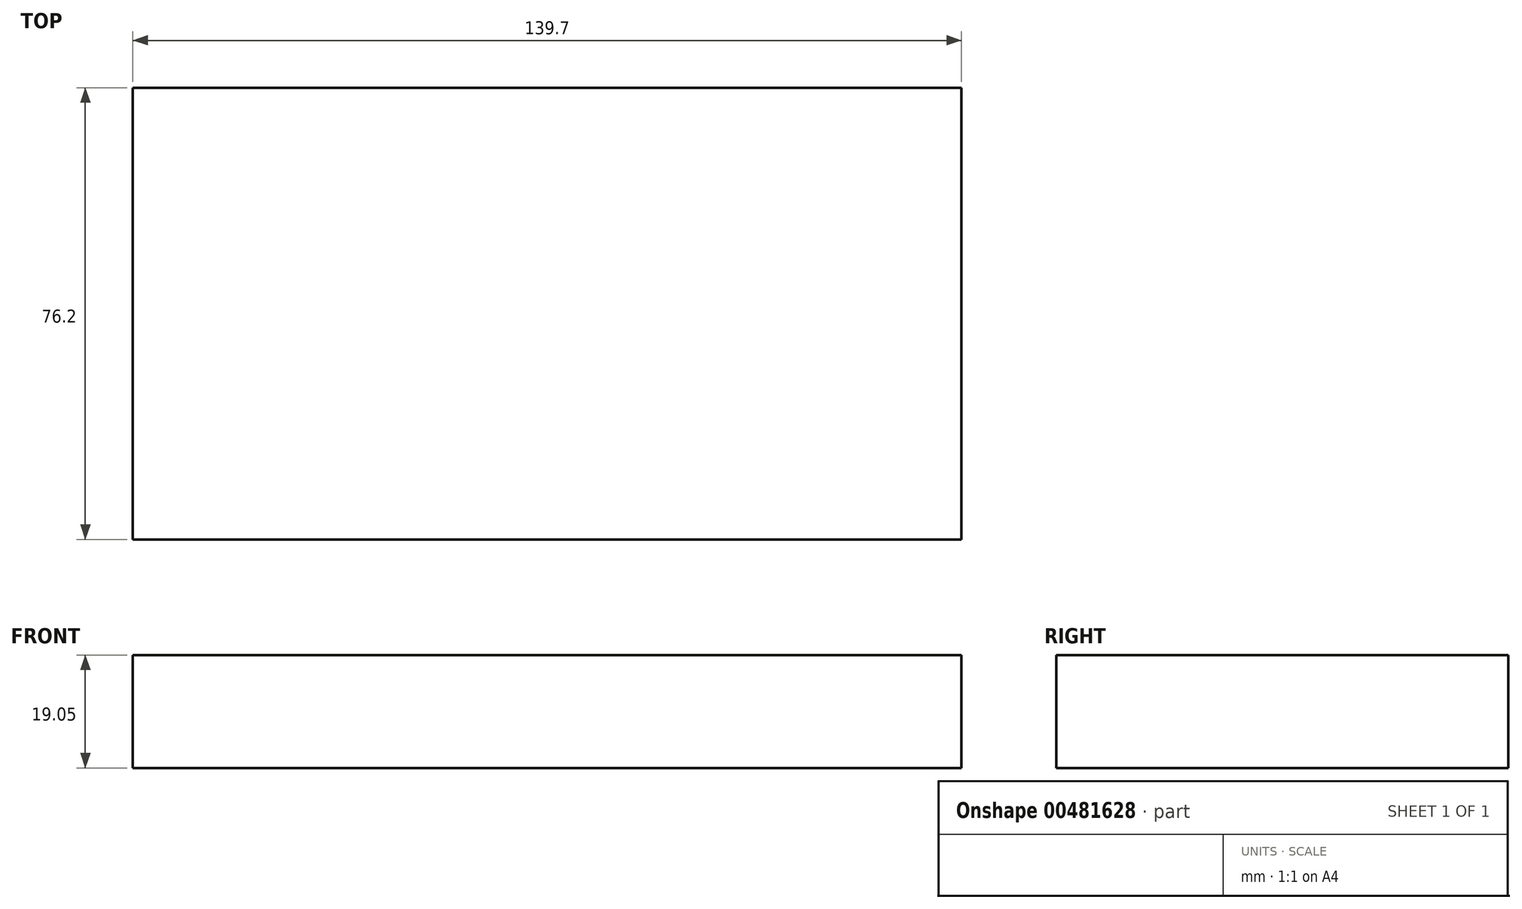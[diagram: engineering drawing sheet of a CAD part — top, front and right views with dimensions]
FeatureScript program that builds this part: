
annotation { "Feature Type Name" : "Feature", "Feature Type Description" : "" }
export const myFeature = defineFeature(function(context is Context, id is Id, definition is map)
    precondition{}
    {
        {
            var Q0;
            Q0=qCreatedBy(makeId("Front.planeOp"),FACE);
            var sketch = newSketch(context, id + "F0", { "sketchPlane" : qUnion([Q0])});
            skLineSegment(sketch, "E0.bottom", {"start": v(-36.14, 4.68) * mm, "end": v(103.56, 4.68) * mm});
            skLineSegment(sketch, "E0.top", {"start": v(-36.14, -14.37) * mm, "end": v(103.56, -14.37) * mm});
            skLineSegment(sketch, "E0.left", {"start": v(-36.14, 4.68) * mm, "end": v(-36.14, -14.37) * mm});
            skLineSegment(sketch, "E0.right", {"start": v(103.56, 4.68) * mm, "end": v(103.56, -14.37) * mm});
            skLineSegment(sketch, "E1.bottom", {"start": v(-36.14, -14.37) * mm, "end": v(-17.1, -14.37) * mm});
            skLineSegment(sketch, "E1.top", {"start": v(-36.14, -27.07) * mm, "end": v(-17.1, -27.07) * mm});
            skLineSegment(sketch, "E1.left", {"start": v(-36.14, -14.37) * mm, "end": v(-36.14, -27.07) * mm});
            skLineSegment(sketch, "E1.right", {"start": v(-17.1, -14.37) * mm, "end": v(-17.1, -27.07) * mm});
            skSolve(sketch);
        }
        {
            var Q0;
            Q0=makeQuery(id+"F0.imprint","IMPRINT",FACE,{"disambiguationData":[TD([[makeQuery(id+"F0.imprint","IMPRINT",EDGE,{"derivedFrom":sQuery(id+"F0.wireOp",EDGE,"E0.bottom")}),-1.0]])]});
            var Q1;
            Q1=makeQuery(id+"F0.imprint","IMPRINT",FACE,{"disambiguationData":[TD([[makeQuery(id+"F0.imprint","IMPRINT",EDGE,{"derivedFrom":sQuery(id+"F0.wireOp",EDGE,"E1.bottom")}),-1.0]])]});
            extrude(context, id + "F1", {"entities" : qUnion([Q0, Q1]), "depth" : 76.2 * mm});
        }
    });
